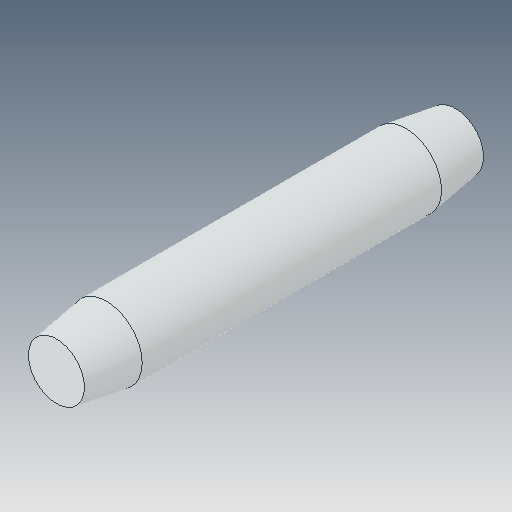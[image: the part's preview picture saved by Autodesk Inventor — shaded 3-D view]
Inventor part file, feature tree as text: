
AUTODESK INVENTOR PART (.ipt)
format: ipt  version: 2023.5 (Build 275446000, 446)  size: 95,232 bytes
history: native  units: in
note: dims shown in document units (in); Inventor stores cm internally (conversion verified against a paired STEP export)
features: chamfer x1
ambient origin geometry x8: Origin, YZ Plane, XZ Plane, XY Plane, X Axis, Y Axis, Z Axis, Center Point
bodies: Solid1 (feature_tree)
feature tree (1):
  chamfer  "Chamfer2"  [1 undecoded]
note: 1 required parameter value undecoded (feature->parameter linkage not recoverable at this tier; creation-order binding heuristic only, values carry confidence <= 0.55)
